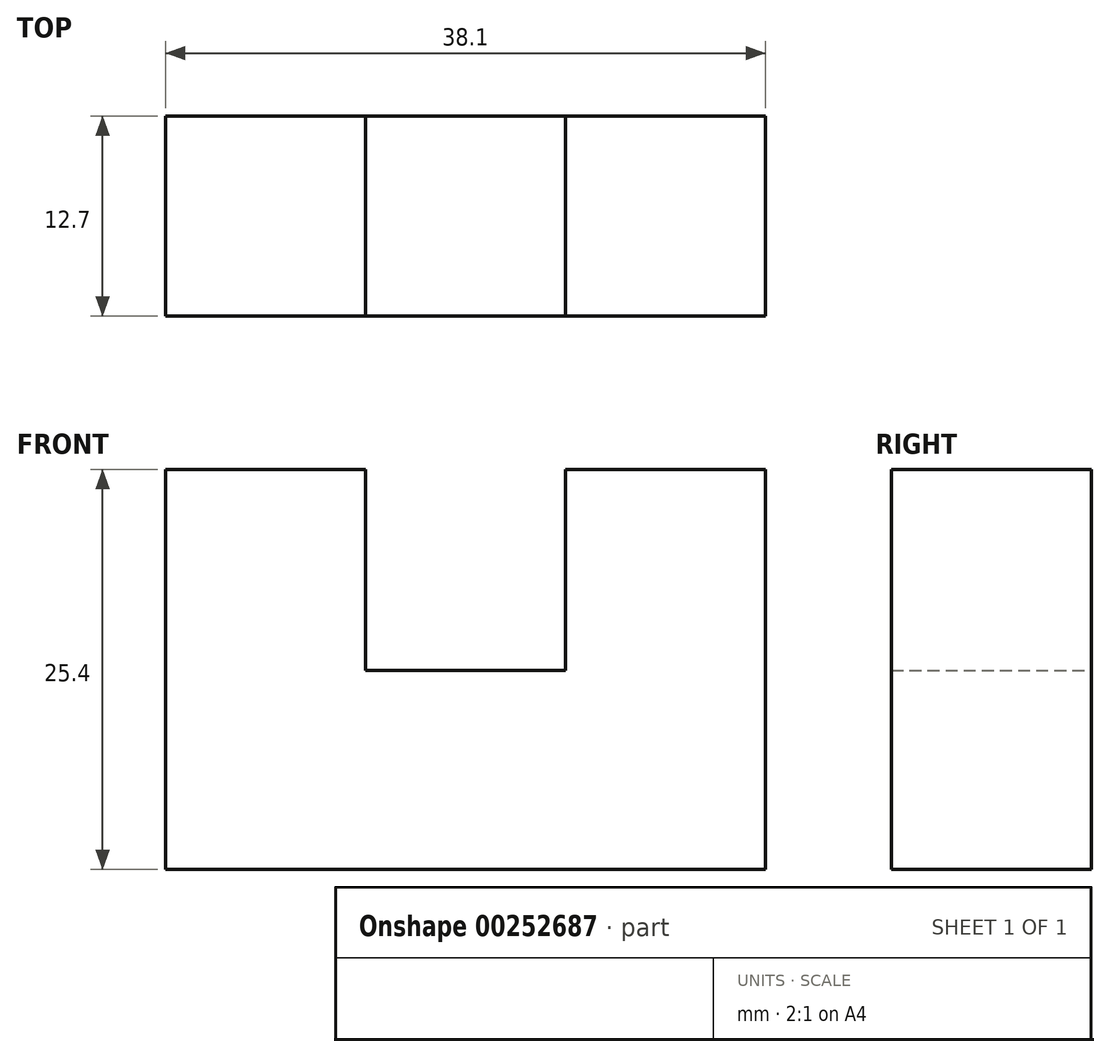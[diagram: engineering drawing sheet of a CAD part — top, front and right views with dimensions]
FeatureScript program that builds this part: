
annotation { "Feature Type Name" : "Feature", "Feature Type Description" : "" }
export const myFeature = defineFeature(function(context is Context, id is Id, definition is map)
    precondition{}
    {
        {
            var Q0;
            Q0=qCreatedBy(makeId("Front.planeOp"),FACE);
            var sketch = newSketch(context, id + "F0", { "sketchPlane" : qUnion([Q0])});
            skLineSegment(sketch, "E0", {"start": v(0, 0) * mm, "end": v(0, 25.4) * mm});
            skLineSegment(sketch, "E1", {"start": v(0, 25.4) * mm, "end": v(12.7, 25.4) * mm});
            skLineSegment(sketch, "E2", {"start": v(12.7, 25.4) * mm, "end": v(12.7, 12.62) * mm});
            skLineSegment(sketch, "E3", {"start": v(12.7, 12.62) * mm, "end": v(25.4, 12.62) * mm});
            skLineSegment(sketch, "E4", {"start": v(25.4, 12.62) * mm, "end": v(25.4, 25.4) * mm});
            skLineSegment(sketch, "E5", {"start": v(25.4, 25.4) * mm, "end": v(38.1, 25.4) * mm});
            skLineSegment(sketch, "E6", {"start": v(38.1, 25.4) * mm, "end": v(38.1, 0) * mm});
            skLineSegment(sketch, "E7", {"start": v(38.1, 0) * mm, "end": v(0, 0) * mm});
            skSolve(sketch);
        }
        {
            var Q0;
            Q0=makeQuery(id+"F0.imprint","IMPRINT",FACE,{"disambiguationData":[TD([[makeQuery(id+"F0.imprint","IMPRINT",EDGE,{"derivedFrom":sQuery(id+"F0.wireOp",EDGE,"E0")}),-1.0]])]});
            extrude(context, id + "F1", {"entities" : qUnion([Q0]), "depth" : 12.7 * mm});
        }
    });
